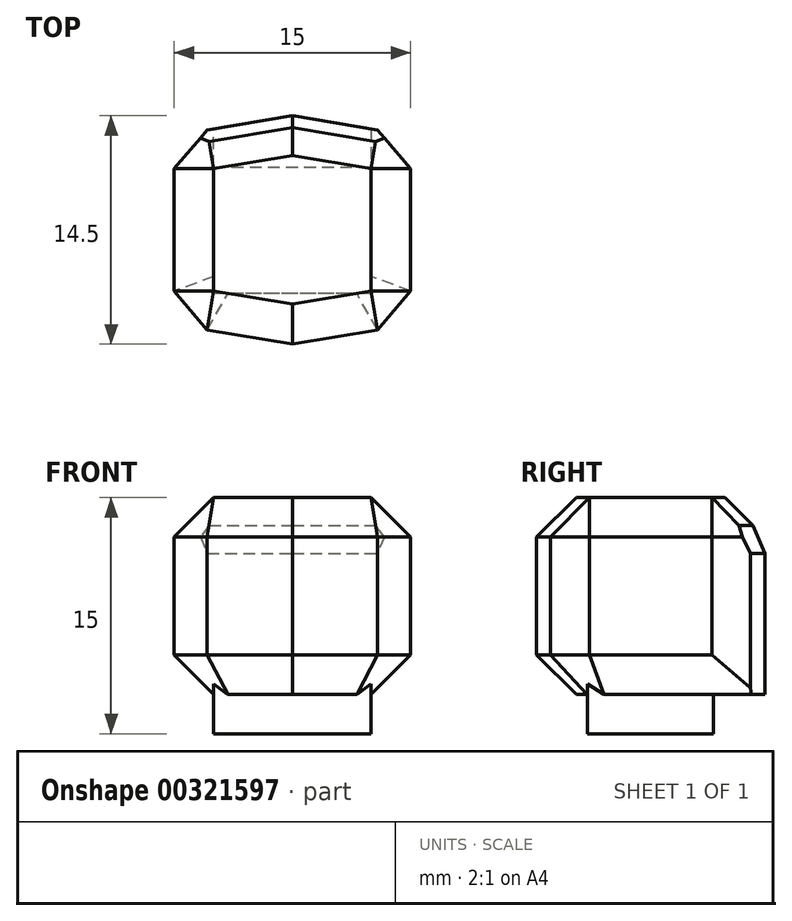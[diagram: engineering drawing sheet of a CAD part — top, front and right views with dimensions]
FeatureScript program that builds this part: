
annotation { "Feature Type Name" : "Feature", "Feature Type Description" : "" }
export const myFeature = defineFeature(function(context is Context, id is Id, definition is map)
    precondition{}
    {
        {
            var Q0;
            Q0=qCreatedBy(makeId("Top.planeOp"),FACE);
            var sketch = newSketch(context, id + "F0", { "sketchPlane" : qUnion([Q0])});
            skLineSegment(sketch, "E0.bottom", {"start": v(-42.96, 20.93) * mm, "end": v(-32.96, 20.93) * mm});
            skLineSegment(sketch, "E0.top", {"start": v(-42.96, 12.93) * mm, "end": v(-32.96, 12.93) * mm});
            skLineSegment(sketch, "E0.left", {"start": v(-42.96, 20.93) * mm, "end": v(-42.96, 12.93) * mm});
            skLineSegment(sketch, "E0.right", {"start": v(-32.96, 20.93) * mm, "end": v(-32.96, 12.93) * mm});
            skLineSegment(sketch, "E1", {"start": v(-37.96, 20.93) * mm, "end": v(-37.96, 12.93) * mm});
            skPoint(sketch, "E1.endSnap0", {"position": v(-37.96, 12.93) * mm});
            skLineSegment(sketch, "E2", {"start": v(-42.96, 12.93) * mm, "end": v(-37.96, 12.93) * mm});
            skLineSegment(sketch, "E3", {"start": v(-32.96, 12.93) * mm, "end": v(-37.96, 12.93) * mm});
            skLineSegment(sketch, "E4", {"start": v(-37.96, 20.93) * mm, "end": v(-37.96, 10.93) * mm});
            skLineSegment(sketch, "E5", {"start": v(-42.96, 12.93) * mm, "end": v(-37.96, 10.93) * mm});
            skLineSegment(sketch, "E6", {"start": v(-32.96, 12.93) * mm, "end": v(-37.96, 10.93) * mm});
            skSolve(sketch);
        }
        {
            var Q0;
            {var subQ0=sQuery(id+"F0.wireOp",EDGE,"E0.left");Q0=makeQuery(id+"F0.imprint","IMPRINT",FACE,{"disambiguationData":[TD([[makeQuery(id+"F0.imprint","IMPRINT",EDGE,{"derivedFrom":subQ0}),1.0]])]});}
            var Q1;
            {var subQ0=sQuery(id+"F0.wireOp",EDGE,"E0.right");Q1=makeQuery(id+"F0.imprint","IMPRINT",FACE,{"disambiguationData":[TD([[makeQuery(id+"F0.imprint","IMPRINT",EDGE,{"derivedFrom":subQ0}),-1.0]])]});}
            var Q2;
            {var subQ0=sQuery(id+"F0.wireOp",EDGE,"E3");Q2=makeQuery(id+"F0.imprint","IMPRINT",FACE,{"disambiguationData":[TD([[makeQuery(id+"F0.imprint","IMPRINT",EDGE,{"derivedFrom":subQ0}),-1.0]])]});}
            var Q3;
            {var subQ0=sQuery(id+"F0.wireOp",EDGE,"E2");Q3=makeQuery(id+"F0.imprint","IMPRINT",FACE,{"disambiguationData":[TD([[makeQuery(id+"F0.imprint","IMPRINT",EDGE,{"derivedFrom":subQ0}),1.0]])]});}
            extrude(context, id + "F1", {"entities" : qUnion([Q0, Q1, Q2, Q3]), "depth" : 2.5 * mm});
        }
        {
            var Q0;
            Q0=makeQuery(id+"F1.opExtrude","CAP_FACE",FACE,{"disambiguationData":[OSD([sQuery(id+"F0.wireOp",EDGE,"E0.bottom"),sQuery(id+"F0.wireOp",EDGE,"E0.left"),sQuery(id+"F0.wireOp",EDGE,"E0.right"),sQuery(id+"F0.wireOp",EDGE,"E2"),sQuery(id+"F0.wireOp",EDGE,"E3")])],"isStart":false});
            var sketch = newSketch(context, id + "F2", { "sketchPlane" : qUnion([Q0])});
            skLineSegment(sketch, "E7", {"start": v(-42.96, 20.93) * mm, "end": v(-32.96, 20.93) * mm});
            skLineSegment(sketch, "E8", {"start": v(-32.96, 20.93) * mm, "end": v(-30.46, 20.93) * mm});
            skLineSegment(sketch, "E9", {"start": v(-42.96, 20.93) * mm, "end": v(-45.46, 20.93) * mm});
            skLineSegment(sketch, "E10", {"start": v(-45.46, 20.93) * mm, "end": v(-45.46, 10.93) * mm});
            skLineSegment(sketch, "E11", {"start": v(-30.46, 20.93) * mm, "end": v(-30.46, 10.93) * mm});
            skLineSegment(sketch, "E12", {"start": v(-37.96, 20.93) * mm, "end": v(-37.96, 9.68) * mm});
            skLineSegment(sketch, "E13", {"start": v(-45.46, 10.93) * mm, "end": v(-37.96, 9.68) * mm});
            skLineSegment(sketch, "E14", {"start": v(-37.96, 9.68) * mm, "end": v(-30.46, 10.93) * mm});
            skLineSegment(sketch, "E15", {"start": v(-37.96, 20.93) * mm, "end": v(-37.96, 24.18) * mm});
            skPoint(sketch, "E16.endSnap0", {"position": v(-42.96, 16.93) * mm});
            skLineSegment(sketch, "E17", {"start": v(-45.46, 20.93) * mm, "end": v(-45.46, 22.93) * mm});
            skLineSegment(sketch, "E18", {"start": v(-45.46, 22.93) * mm, "end": v(-37.96, 24.18) * mm});
            skLineSegment(sketch, "E19", {"start": v(-30.46, 20.93) * mm, "end": v(-30.46, 22.93) * mm});
            skLineSegment(sketch, "E20", {"start": v(-37.96, 24.18) * mm, "end": v(-30.46, 22.93) * mm});
            skSolve(sketch);
        }
        {
            var Q0;
            Q0=makeQuery(id+"F2.imprint","IMPRINT",FACE,{"disambiguationData":[TD([[makeQuery(id+"F2.imprint","IMPRINT",EDGE,{"derivedFrom":sQuery(id+"F2.wireOp",EDGE,"E9")}),1.0]])]});
            var Q1;
            {var subQ1=makeQuery(id+"F1.opExtrude","CAP_EDGE",EDGE,{"disambiguationData":[OSD([sQuery(id+"F0.wireOp",EDGE,"E0.left")])],"isStart":false});Q1=makeQuery(id+"F2.imprint","IMPRINT",FACE,{"disambiguationData":[TD([[makeQuery(id+"F2.imprint","IMPRINT",EDGE,{"derivedFrom":subQ1}),1.0]])]});}
            var Q2;
            {var subQ1=makeQuery(id+"F1.opExtrude","CAP_EDGE",EDGE,{"disambiguationData":[OSD([sQuery(id+"F0.wireOp",EDGE,"E0.right")])],"isStart":false});Q2=makeQuery(id+"F2.imprint","IMPRINT",FACE,{"disambiguationData":[TD([[makeQuery(id+"F2.imprint","IMPRINT",EDGE,{"derivedFrom":subQ1}),-1.0]])]});}
            var Q3;
            Q3=makeQuery(id+"F2.imprint","IMPRINT",FACE,{"disambiguationData":[TD([[makeQuery(id+"F2.imprint","IMPRINT",EDGE,{"derivedFrom":sQuery(id+"F2.wireOp",EDGE,"E8")}),-1.0]])]});
            var Q4;
            {var subQ0=sQuery(id+"F2.wireOp",EDGE,"E9");Q4=makeQuery(id+"F2.imprint","IMPRINT",FACE,{"disambiguationData":[TD([[makeQuery(id+"F2.imprint","IMPRINT",EDGE,{"derivedFrom":subQ0}),-1.0]])]});}
            var Q5;
            {var subQ0=sQuery(id+"F2.wireOp",EDGE,"E8");Q5=makeQuery(id+"F2.imprint","IMPRINT",FACE,{"disambiguationData":[TD([[makeQuery(id+"F2.imprint","IMPRINT",EDGE,{"derivedFrom":subQ0}),1.0]])]});}
            extrude(context, id + "F3", {"entities" : qUnion([Q0, Q1, Q2, Q3, Q4, Q5]), "operationType" : NewBodyOperationType.ADD, "depth" : 12.5 * mm});
        }
        {
            var Q0;
            Q0=makeQuery(id+"F3.opExtrude","CAP_EDGE",EDGE,{"disambiguationData":[OSD([sQuery(id+"F2.wireOp",EDGE,"E14")])],"isStart":false});
            var Q1;
            Q1=makeQuery(id+"F3.opExtrude","CAP_EDGE",EDGE,{"disambiguationData":[OSD([sQuery(id+"F2.wireOp",EDGE,"E13")])],"isStart":false});
            var Q2;
            Q2=makeQuery(id+"F3.opExtrude","SWEPT_EDGE",EDGE,{"disambiguationData":[OSD([sQuery(id+"F2.wireOp",EDGE,"E11"),sQuery(id+"F2.wireOp",EDGE,"E14")])]});
            var Q3;
            Q3=makeQuery(id+"F3.opExtrude","SWEPT_EDGE",EDGE,{"disambiguationData":[OSD([sQuery(id+"F2.wireOp",EDGE,"E10"),sQuery(id+"F2.wireOp",EDGE,"E13")])]});
            var Q4;
            Q4=makeQuery(id+"F3.opExtrude","CAP_EDGE",EDGE,{"disambiguationData":[OSD([sQuery(id+"F2.wireOp",EDGE,"E11")])],"isStart":false});
            var Q5;
            Q5=makeQuery(id+"F3.opExtrude","CAP_EDGE",EDGE,{"disambiguationData":[OSD([sQuery(id+"F2.wireOp",EDGE,"E10"),sQuery(id+"F2.wireOp",EDGE,"E17")])],"isStart":false});
            var Q6;
            Q6=makeQuery(id+"F3.opExtrude","SWEPT_EDGE",EDGE,{"disambiguationData":[OSD([sQuery(id+"F2.wireOp",EDGE,"E17"),sQuery(id+"F2.wireOp",EDGE,"E18")])]});
            var Q7;
            Q7=makeQuery(id+"F3.opExtrude","SWEPT_EDGE",EDGE,{"disambiguationData":[OSD([sQuery(id+"F2.wireOp",EDGE,"E19"),sQuery(id+"F2.wireOp",EDGE,"E20")])]});
            var Q8;
            Q8=makeQuery(id+"F3.opExtrude","CAP_EDGE",EDGE,{"disambiguationData":[OSD([sQuery(id+"F2.wireOp",EDGE,"E20")])],"isStart":false});
            var Q9;
            Q9=makeQuery(id+"F3.opExtrude","CAP_EDGE",EDGE,{"disambiguationData":[OSD([sQuery(id+"F2.wireOp",EDGE,"E18")])],"isStart":false});
            chamfer(context, id + "F4", {"entities" : qUnion([Q0, Q1, Q2, Q3, Q4, Q5, Q6, Q7, Q8, Q9]), "width" : 2.5 * mm, "tangentPropagation" : true});
        }
        {
            var Q0;
            Q0=makeQuery(id+"F3.opExtrude","CAP_EDGE",EDGE,{"disambiguationData":[OSD([sQuery(id+"F2.wireOp",EDGE,"E13")])],"isStart":true});
            var Q1;
            Q1=makeQuery(id+"F3.opExtrude","CAP_EDGE",EDGE,{"disambiguationData":[OSD([sQuery(id+"F2.wireOp",EDGE,"E14")])],"isStart":true});
            var Q2;
            Q2=makeQuery(id+"F3.opExtrude","CAP_EDGE",EDGE,{"disambiguationData":[OSD([sQuery(id+"F2.wireOp",EDGE,"E10")])],"isStart":true});
            var Q3;
            {var subQ0=sQuery(id+"F2.wireOp",EDGE,"E13");var subQ1=sQuery(id+"F2.wireOp",EDGE,"E10");Q3=makeQuery(id+"F4.opChamfer","BLEND_EDGE",EDGE,{"blendedFrom":[makeQuery(id+"F3.opExtrude","SWEPT_EDGE",EDGE,{"disambiguationData":[OSD([subQ1,subQ0])]}),makeQuery(id+"F3.opExtrude","CAP_FACE",FACE,{"disambiguationData":[OSD([sQuery(id+"F2.wireOp",EDGE,"E7"),sQuery(id+"F2.wireOp",EDGE,"E8"),sQuery(id+"F2.wireOp",EDGE,"E9"),subQ1,sQuery(id+"F2.wireOp",EDGE,"E11"),subQ0,sQuery(id+"F2.wireOp",EDGE,"E14")])],"isStart":true})],"blendedInto":[makeQuery(id+"F3.opExtrude","CAP_FACE",FACE,{"disambiguationData":[OSD([sQuery(id+"F2.wireOp",EDGE,"E7"),sQuery(id+"F2.wireOp",EDGE,"E8"),sQuery(id+"F2.wireOp",EDGE,"E9"),subQ1,sQuery(id+"F2.wireOp",EDGE,"E11"),subQ0,sQuery(id+"F2.wireOp",EDGE,"E14")])],"isStart":true})]});}
            var Q4;
            {var subQ0=sQuery(id+"F2.wireOp",EDGE,"E14");var subQ1=sQuery(id+"F2.wireOp",EDGE,"E11");Q4=makeQuery(id+"F4.opChamfer","BLEND_EDGE",EDGE,{"blendedFrom":[makeQuery(id+"F3.opExtrude","SWEPT_EDGE",EDGE,{"disambiguationData":[OSD([subQ1,subQ0])]}),makeQuery(id+"F3.opExtrude","CAP_FACE",FACE,{"disambiguationData":[OSD([sQuery(id+"F2.wireOp",EDGE,"E7"),sQuery(id+"F2.wireOp",EDGE,"E8"),sQuery(id+"F2.wireOp",EDGE,"E9"),sQuery(id+"F2.wireOp",EDGE,"E10"),subQ1,sQuery(id+"F2.wireOp",EDGE,"E13"),subQ0])],"isStart":true})],"blendedInto":[makeQuery(id+"F3.opExtrude","CAP_FACE",FACE,{"disambiguationData":[OSD([sQuery(id+"F2.wireOp",EDGE,"E7"),sQuery(id+"F2.wireOp",EDGE,"E8"),sQuery(id+"F2.wireOp",EDGE,"E9"),sQuery(id+"F2.wireOp",EDGE,"E10"),subQ1,sQuery(id+"F2.wireOp",EDGE,"E13"),subQ0])],"isStart":true})]});}
            var Q5;
            Q5=makeQuery(id+"F3.opExtrude","CAP_EDGE",EDGE,{"disambiguationData":[OSD([sQuery(id+"F2.wireOp",EDGE,"E11")])],"isStart":true});
            var Q6;
            {var subQ0=sQuery(id+"F2.wireOp",EDGE,"E18");Q6=makeQuery(id+"F4.opChamfer","BLEND_EDGE",EDGE,{"blendedFrom":[makeQuery(id+"F3.opExtrude","CAP_EDGE",EDGE,{"disambiguationData":[OSD([subQ0])],"isStart":false}),makeQuery(id+"F3.opExtrude","SWEPT_FACE",FACE,{"disambiguationData":[OSD([subQ0])]})],"blendedInto":[makeQuery(id+"F3.opExtrude","SWEPT_FACE",FACE,{"disambiguationData":[OSD([subQ0])]})]});}
            var Q7;
            {var subQ0=sQuery(id+"F2.wireOp",EDGE,"E20");Q7=makeQuery(id+"F4.opChamfer","BLEND_EDGE",EDGE,{"blendedFrom":[makeQuery(id+"F3.opExtrude","CAP_EDGE",EDGE,{"disambiguationData":[OSD([subQ0])],"isStart":false}),makeQuery(id+"F3.opExtrude","SWEPT_FACE",FACE,{"disambiguationData":[OSD([subQ0])]})],"blendedInto":[makeQuery(id+"F3.opExtrude","SWEPT_FACE",FACE,{"disambiguationData":[OSD([subQ0])]})]});}
            chamfer(context, id + "F5", {"entities" : qUnion([Q0, Q1, Q2, Q3, Q4, Q5, Q6, Q7]), "width" : 2.5 * mm, "tangentPropagation" : true});
        }
    });
